# Revit family: Hager-Vega-IP40-syst-BE-fr
name_source: partatom
category: Electrical Equipment
units: mm (PartAtom-declared; Revit-internal decimal feet)

## family parameters
Cut with Voids When Loaded = No
Host = Face
Panel Configuration = Two Columns, Circuits Across
Part Type = Panelboard
Room Calculation Point = No
Round Connector Dimension = Use Diameter
Shared = No

## types (14) — shared parameters
EF000003 - mode de pose = EV000384 - saillie
EF000007 - couleur = EV000202 - blanc
EF000008 - largeur = 400 mm  [stored 1.31234 ft]
EF000049 - profondeur = 146 mm  [stored 0.479003 ft]
EF000116 - numéro RAL = 9010
EF000339 - type de capot = EV004216 - porte
EF001062 - finition CEM = No
EF001088 - possibilité de montage en saillie = Yes
EF001134 - rail DIN = Yes
EF001596 - matériau du boîtier/corps = EV000139 - plastique
EF002950 - largeur en nombre de modules = 18
EF004462 - type de fermeture = EV000154 - autre
EF006306 - avec serrure = No
EF015777 - borne à conducteur neutre = No
EF015941 - porte pour transmission du signal = Yes
HG000001 - nombre de colonnes = 1
HG000002 - avec porte = Yes
HG000003 - Gamme = Vega
HG000005 - Epaisseur = 3 mm  [stored 0.00984252 ft]
HG000006 - Encastré = No
HG000009 - Porte à double battant = No
HG000010 - Portes asymétriques = No
HG000017 - Distance entre pôles = 18 mm  [stored 0.0590551 ft]
Manufacturer = Hager
Type Comments = Vega
zero-valued in all types: Default Elevation, EF000218 - profondeur d'encastrement, EF000332 - hauteur d'encastrement, EF000846 - largeur d'encastrement, HG000007 - Nombre de colonnes vides

## per-type parameters (varying)
| type | EF000040 - hauteur | EF000118 - avec cadre/support de montage | EF000266 - nombre de rangées | EF001131 - profondeur intérieure | EF005474 - indice de protection (IP) | EF006244 - couvercle/porte transparent(e) | EF009212 - finition du couvercle | EF015776 - borne de mise à la terre | HG000004 - Référence fabricant | HG000008 - Nombre de rangées vides | HG000011 - Rangées du bas vides | Model |
| Saillie IP40 L400 H325 P146 18 Modules - VB118B | 325 mm  [stored 1.06627 ft] | No | 1 | 120 mm  [stored 0.393701 ft] | EV006415 - IP40 | No | EV000116 - fermé | Yes | VB118B | 0 | No | VB118B |
| Saillie IP40 L400 H325 P146 18 Modules - VB118R | 325 mm  [stored 1.06627 ft] | No | 1 | 120 mm  [stored 0.393701 ft] | EV006415 - IP40 | Yes | EV000116 - fermé | Yes | VB118R | 0 | No | VB118R |
| Saillie IP40 L400 H475 P146 18 Modules - VB218B | 475 mm  [stored 1.5584 ft] | No | 2 | 120 mm  [stored 0.393701 ft] | EV006415 - IP40 | No | EV000116 - fermé | Yes | VB218B | 0 | No | VB218B |
| Saillie IP40 L400 H475 P146 18 Modules - VB218R | 475 mm  [stored 1.5584 ft] | No | 2 | 120 mm  [stored 0.393701 ft] | EV006415 - IP40 | Yes | EV000116 - fermé | Yes | VB218R | 0 | No | VB218R |
| Saillie IP40 L400 H625 P146 18 Modules - VB318B | 625 mm  [stored 2.05052 ft] | No | 3 | 120 mm  [stored 0.393701 ft] | EV006415 - IP40 | No | EV000116 - fermé | Yes | VB318B | 0 | No | VB318B |
| Saillie IP40 L400 H625 P146 18 Modules - VB318R | 625 mm  [stored 2.05052 ft] | No | 3 | 120 mm  [stored 0.393701 ft] | EV006415 - IP40 | Yes | EV000116 - fermé | Yes | VB318R | 0 | No | VB318R |
| Saillie IP40 L400 H775 P146 18 Modules - VB418B | 775 mm  [stored 2.54265 ft] | No | 4 | 120 mm  [stored 0.393701 ft] | EV006415 - IP40 | No | EV000116 - fermé | Yes | VB418B | 0 | No | VB418B |
| Saillie IP40 L400 H775 P146 18 Modules - VB418R | 775 mm  [stored 2.54265 ft] | No | 4 | 120 mm  [stored 0.393701 ft] | EV006415 - IP40 | Yes | EV000116 - fermé | Yes | VB418R | 0 | No | VB418R |
| Saillie utre L400 H625 P146 18 Modules - VB318MMP | 625 mm  [stored 2.05052 ft] | Yes | 1 | 140 mm  [stored 0.459318 ft] | EV000154 - autre | No | EV009916 - avec échancrure | No | VB318MMP | 2 | Yes | VB318MMP |
| Saillie utre L400 H625 P146 18 Modules - VB318MMT | 625 mm  [stored 2.05052 ft] | Yes | 1 | 140 mm  [stored 0.459318 ft] | EV000154 - autre | Yes | EV009916 - avec échancrure | No | VB318MMT | 2 | Yes | VB318MMT |
| Saillie utre L400 H775 P146 18 Modules - VB418MMP | 775 mm  [stored 2.54265 ft] | Yes | 1 | 140 mm  [stored 0.459318 ft] | EV000154 - autre | No | EV009916 - avec échancrure | No | VB418MMP | 3 | Yes | VB418MMP |
| Saillie utre L400 H775 P146 18 Modules - VB418MMT | 775 mm  [stored 2.54265 ft] | Yes | 1 | 140 mm  [stored 0.459318 ft] | EV000154 - autre | Yes | EV009916 - avec échancrure | No | VB418MMT | 3 | Yes | VB418MMT |
| Saillie utre L400 H775 P146 18 Modules - VB418MTP | 775 mm  [stored 2.54265 ft] | Yes | 2 | 140 mm  [stored 0.459318 ft] | EV000154 - autre | Yes | EV009916 - avec échancrure | No | VB418MTP | 2 | Yes | VB418MTP |
| Saillie utre L400 H775 P146 18 Modules - VB418MTT | 775 mm  [stored 2.54265 ft] | Yes | 2 | 140 mm  [stored 0.459318 ft] | EV000154 - autre | Yes | EV009916 - avec échancrure | No | VB418MTT | 2 | Yes | VB418MTT |

note: [stored X ft] marks values corroborated as IEEE doubles in the binary element streams (Revit-internal decimal feet)

## geometry (parser evidence)
native form markers: Sweep x17
no freeform markers — native parametric forms only
